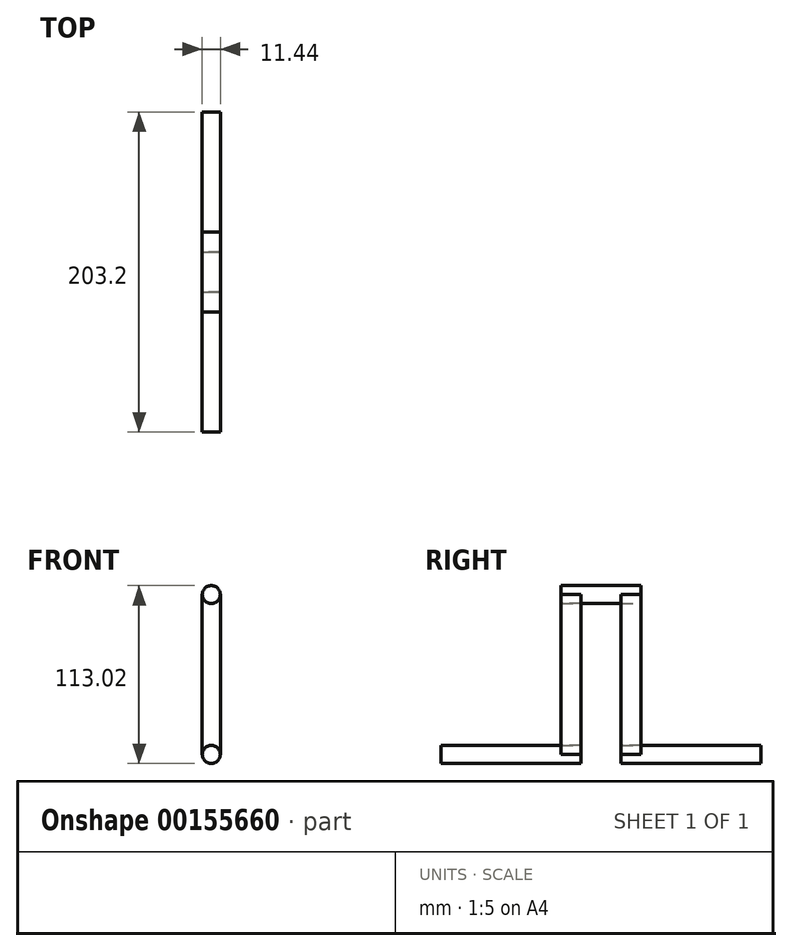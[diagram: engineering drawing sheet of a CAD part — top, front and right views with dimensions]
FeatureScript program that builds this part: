
annotation { "Feature Type Name" : "Feature", "Feature Type Description" : "" }
export const myFeature = defineFeature(function(context is Context, id is Id, definition is map)
    precondition{}
    {
        {
            var Q0;
            Q0=qCreatedBy(makeId("Front.planeOp"),FACE);
            var sketch = newSketch(context, id + "F0", { "sketchPlane" : qUnion([Q0])});
            skCircle(sketch, "E0", {"center": v(0, 0) * mm, "radius": 5.72 * mm});
            skSolve(sketch);
        }
        {
            var Q0;
            Q0=makeQuery(id+"F0.imprint","IMPRINT",FACE,{"disambiguationData":[TD([[makeQuery(id+"F0.imprint","IMPRINT",EDGE,{"derivedFrom":sQuery(id+"F0.wireOp",EDGE,"E0")}),1.0]])]});
            extrude(context, id + "F1", {"entities" : qUnion([Q0]), "endBound" : BoundingType.SYMMETRIC, "depth" : 50.8 * mm});
        }
        {
            var Q0;
            Q0=makeQuery(id+"F1.opExtrude","CAP_FACE",FACE,{"disambiguationData":[OSD([sQuery(id+"F0.wireOp",EDGE,"E0")])],"isStart":false});
            var sketch = newSketch(context, id + "F2", { "sketchPlane" : qUnion([Q0])});
            skLineSegment(sketch, "E1.bottom", {"start": v(-5.72, 0) * mm, "end": v(5.71, 0) * mm});
            skLineSegment(sketch, "E1.top", {"start": v(-5.71, -101.6) * mm, "end": v(5.72, -101.6) * mm});
            skLineSegment(sketch, "E1.left", {"start": v(-5.72, 0) * mm, "end": v(-5.72, -101.6) * mm});
            skLineSegment(sketch, "E1.right", {"start": v(5.72, 0) * mm, "end": v(5.72, -101.6) * mm});
            skSolve(sketch);
        }
        {
            var Q0;
            Q0=makeQuery(id+"F2.imprint","IMPRINT",FACE,{"disambiguationData":[TD([[makeQuery(id+"F2.imprint","IMPRINT",EDGE,{"derivedFrom":sQuery(id+"F2.wireOp",EDGE,"E1.top")}),1.0]])]});
            extrude(context, id + "F3", {"entities" : qUnion([Q0]), "depth" : 12.7 * mm});
        }
        {
            var Q0;
            Q0=makeQuery(id+"F1.opExtrude","CAP_FACE",FACE,{"disambiguationData":[OSD([sQuery(id+"F0.wireOp",EDGE,"E0")])],"isStart":true});
            var sketch = newSketch(context, id + "F4", { "sketchPlane" : qUnion([Q0])});
            skLineSegment(sketch, "E2.bottom", {"start": v(-5.72, 0) * mm, "end": v(5.71, 0) * mm});
            skLineSegment(sketch, "E2.top", {"start": v(-5.71, -101.6) * mm, "end": v(5.72, -101.6) * mm});
            skLineSegment(sketch, "E2.left", {"start": v(-5.72, 0) * mm, "end": v(-5.72, -101.6) * mm});
            skLineSegment(sketch, "E2.right", {"start": v(5.72, 0) * mm, "end": v(5.72, -101.6) * mm});
            skSolve(sketch);
        }
        {
            var Q0;
            Q0=makeQuery(id+"F4.imprint","IMPRINT",FACE,{"disambiguationData":[TD([[makeQuery(id+"F4.imprint","IMPRINT",EDGE,{"derivedFrom":sQuery(id+"F4.wireOp",EDGE,"E2.top")}),1.0]])]});
            extrude(context, id + "F5", {"entities" : qUnion([Q0]), "depth" : 12.7 * mm});
        }
        {
            var Q0;
            Q0=makeQuery(id+"F5.opExtrude","SWEPT_BODY",BODY,{"disambiguationData":[OSD([sQuery(id+"F0.wireOp",EDGE,"E0"),sQuery(id+"F4.wireOp",EDGE,"E2.top"),sQuery(id+"F4.wireOp",EDGE,"E2.left"),sQuery(id+"F4.wireOp",EDGE,"E2.right")])]});
            var Q1;
            Q1=makeQuery(id+"F5.opExtrude","CAP_FACE",FACE,{"disambiguationData":[OSD([sQuery(id+"F0.wireOp",EDGE,"E0"),sQuery(id+"F4.wireOp",EDGE,"E2.top"),sQuery(id+"F4.wireOp",EDGE,"E2.left"),sQuery(id+"F4.wireOp",EDGE,"E2.right")])],"isStart":true});
            mirror(context, id + "F6", {"entities" : qUnion([Q0]), "mirrorPlane" : qUnion([Q1])});
        }
        {
            var Q0;
            Q0=makeQuery(id+"F5.opExtrude","SWEPT_BODY",BODY,{"disambiguationData":[OSD([sQuery(id+"F0.wireOp",EDGE,"E0"),sQuery(id+"F4.wireOp",EDGE,"E2.top"),sQuery(id+"F4.wireOp",EDGE,"E2.left"),sQuery(id+"F4.wireOp",EDGE,"E2.right")])]});
            deleteBodies(context, id + "F7", {"entities" : qUnion([Q0])});
        }
        {
            var Q0;
            Q0=makeQuery(id+"F3.opExtrude","SWEPT_BODY",BODY,{"disambiguationData":[OSD([sQuery(id+"F0.wireOp",EDGE,"E0"),sQuery(id+"F2.wireOp",EDGE,"E1.top"),sQuery(id+"F2.wireOp",EDGE,"E1.left"),sQuery(id+"F2.wireOp",EDGE,"E1.right")])]});
            var Q1;
            Q1=makeQuery(id+"F3.opExtrude","CAP_FACE",FACE,{"disambiguationData":[OSD([sQuery(id+"F0.wireOp",EDGE,"E0"),sQuery(id+"F2.wireOp",EDGE,"E1.top"),sQuery(id+"F2.wireOp",EDGE,"E1.left"),sQuery(id+"F2.wireOp",EDGE,"E1.right")])],"isStart":true});
            mirror(context, id + "F8", {"entities" : qUnion([Q0]), "mirrorPlane" : qUnion([Q1])});
        }
        {
            var Q0;
            Q0=makeQuery(id+"F3.opExtrude","SWEPT_BODY",BODY,{"disambiguationData":[OSD([sQuery(id+"F0.wireOp",EDGE,"E0"),sQuery(id+"F2.wireOp",EDGE,"E1.top"),sQuery(id+"F2.wireOp",EDGE,"E1.left"),sQuery(id+"F2.wireOp",EDGE,"E1.right")])]});
            deleteBodies(context, id + "F9", {"entities" : qUnion([Q0])});
        }
        {
            var Q0;
            Q0=qCreatedBy(makeId("Front.planeOp"),FACE);
            var sketch = newSketch(context, id + "F10", { "sketchPlane" : qUnion([Q0])});
            skCircle(sketch, "E3", {"center": v(0, -101.59) * mm, "radius": 5.72 * mm});
            skSolve(sketch);
        }
        {
            var Q0;
            Q0=makeQuery(id+"F10.imprint","IMPRINT",FACE,{"disambiguationData":[TD([[makeQuery(id+"F10.imprint","IMPRINT",EDGE,{"derivedFrom":sQuery(id+"F10.wireOp",EDGE,"E3")}),1.0]])]});
            extrude(context, id + "F11", {"entities" : qUnion([Q0]), "operationType" : NewBodyOperationType.REMOVE, "endBound" : BoundingType.SYMMETRIC, "oppositeDirection" : true, "depth" : 101.6 * mm});
        }
        {
            var Q0;
            Q0=makeQuery(id+"F10.imprint","IMPRINT",FACE,{"disambiguationData":[TD([[makeQuery(id+"F10.imprint","IMPRINT",EDGE,{"derivedFrom":sQuery(id+"F10.wireOp",EDGE,"E3")}),1.0]])]});
            extrude(context, id + "F12", {"entities" : qUnion([Q0]), "endBound" : BoundingType.SYMMETRIC, "depth" : 203.2 * mm});
        }
        {
            var Q0;
            Q0=qCreatedBy(makeId("Right.planeOp"),FACE);
            var sketch = newSketch(context, id + "F13", { "sketchPlane" : qUnion([Q0])});
            skLineSegment(sketch, "E4", {"start": v(0, 0) * mm, "end": v(0, -101.6) * mm});
            skLineSegment(sketch, "E5.bottom", {"start": v(12.7, -107.95) * mm, "end": v(-12.7, -107.95) * mm});
            skLineSegment(sketch, "E5.top", {"start": v(12.7, -95.25) * mm, "end": v(-12.7, -95.25) * mm});
            skLineSegment(sketch, "E5.left", {"start": v(12.7, -107.95) * mm, "end": v(12.7, -95.25) * mm});
            skLineSegment(sketch, "E5.right", {"start": v(-12.7, -107.95) * mm, "end": v(-12.7, -95.25) * mm});
            skPoint(sketch, "E5.middle", {"position": v(0, -101.6) * mm});
            skSolve(sketch);
        }
        {
            var Q0;
            Q0 = qSketchRegion(id + "F13", true);
            extrude(context, id + "F14", {"entities" : qUnion([Q0]), "operationType" : NewBodyOperationType.REMOVE, "endBound" : BoundingType.SYMMETRIC, "oppositeDirection" : true, "depth" : 25.4 * mm});
        }
        {
            var Q0;
            Q0 = qSketchRegion(id + "F13", true);
            extrude(context, id + "F15", {"entities" : qUnion([Q0]), "operationType" : NewBodyOperationType.REMOVE, "endBound" : BoundingType.SYMMETRIC, "oppositeDirection" : true, "depth" : 25.4 * mm});
        }
    });
